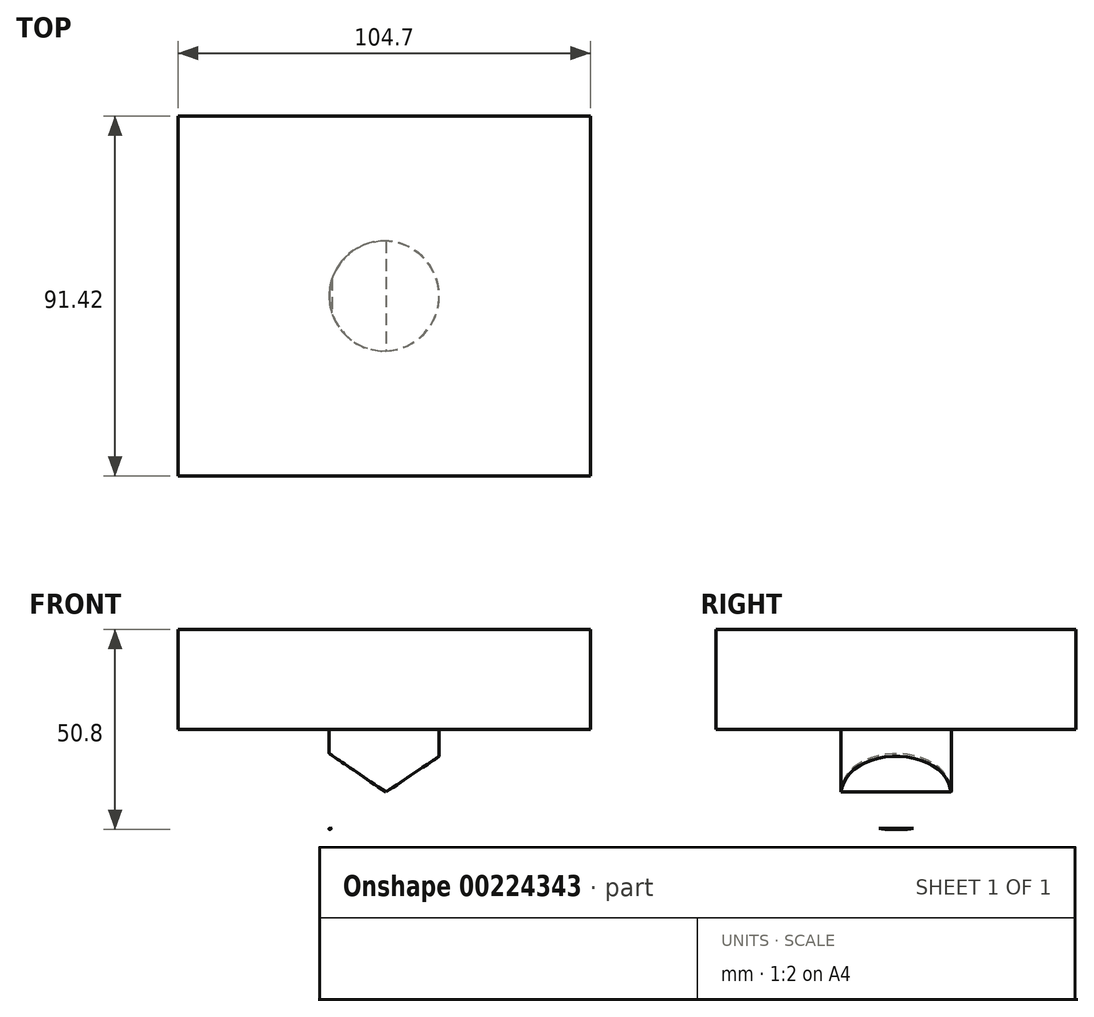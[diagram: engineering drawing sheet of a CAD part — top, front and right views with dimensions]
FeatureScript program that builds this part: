
annotation { "Feature Type Name" : "Feature", "Feature Type Description" : "" }
export const myFeature = defineFeature(function(context is Context, id is Id, definition is map)
    precondition{}
    {
        {
            var Q0;
            Q0=qCreatedBy(makeId("Top.planeOp"),FACE);
            var sketch = newSketch(context, id + "F0", { "sketchPlane" : qUnion([Q0])});
            skLineSegment(sketch, "E0.bottom", {"start": v(52.35, 45.7) * mm, "end": v(-52.35, 45.7) * mm});
            skLineSegment(sketch, "E0.top", {"start": v(52.35, -45.7) * mm, "end": v(-52.35, -45.7) * mm});
            skLineSegment(sketch, "E0.left", {"start": v(52.35, 45.7) * mm, "end": v(52.35, -45.7) * mm});
            skLineSegment(sketch, "E0.right", {"start": v(-52.35, 45.7) * mm, "end": v(-52.35, -45.7) * mm});
            skPoint(sketch, "E0.middle", {"position": v(0, 0) * mm});
            skSolve(sketch);
        }
        {
            var Q0;
            Q0=makeQuery(id+"F0.imprint","IMPRINT",FACE,{"disambiguationData":[TD([[makeQuery(id+"F0.imprint","IMPRINT",EDGE,{"derivedFrom":sQuery(id+"F0.wireOp",EDGE,"E0.bottom")}),1.0]])]});
            extrude(context, id + "F1", {"entities" : qUnion([Q0]), "depth" : 25.4 * mm});
        }
        {
            var Q0;
            Q0=makeQuery(id+"F1.opExtrude","CAP_FACE",FACE,{"disambiguationData":[OSD([sQuery(id+"F0.wireOp",EDGE,"E0.bottom"),sQuery(id+"F0.wireOp",EDGE,"E0.top"),sQuery(id+"F0.wireOp",EDGE,"E0.left"),sQuery(id+"F0.wireOp",EDGE,"E0.right")])],"isStart":true});
            var sketch = newSketch(context, id + "F2", { "sketchPlane" : qUnion([Q0])});
            skCircle(sketch, "E1", {"center": v(0, 0) * mm, "radius": 13.98 * mm});
            skSolve(sketch);
        }
        {
            var Q0;
            Q0 = qSketchRegion(id + "F2", true);
            extrude(context, id + "F3", {"entities" : qUnion([Q0]), "operationType" : NewBodyOperationType.ADD, "depth" : 25.4 * mm});
        }
        {
            var Q0;
            Q0=makeQuery(id+"F1.opExtrude","SWEPT_FACE",FACE,{"disambiguationData":[OSD([sQuery(id+"F0.wireOp",EDGE,"E0.top")])]});
            var sketch = newSketch(context, id + "F4", { "sketchPlane" : qUnion([Q0])});
            skLineSegment(sketch, "E2", {"start": v(13.88, -25.08) * mm, "end": v(-14.08, -6.05) * mm});
            skLineSegment(sketch, "E3", {"start": v(13.88, -25.08) * mm, "end": v(-14.08, -25.08) * mm});
            skLineSegment(sketch, "E4", {"start": v(-14.08, -25.08) * mm, "end": v(-14.08, -6.05) * mm});
            skSolve(sketch);
        }
        {
            var Q0;
            Q0=makeQuery(id+"F4.imprint","IMPRINT",FACE,{"disambiguationData":[TD([[makeQuery(id+"F4.imprint","IMPRINT",EDGE,{"derivedFrom":sQuery(id+"F4.wireOp",EDGE,"E2")}),1.0]])]});
            extrude(context, id + "F5", {"entities" : qUnion([Q0]), "operationType" : NewBodyOperationType.REMOVE, "endBound" : BoundingType.SYMMETRIC, "oppositeDirection" : true, "depth" : 127 * mm});
        }
        {
            var Q0;
            Q0=makeQuery(id+"F1.opExtrude","SWEPT_FACE",FACE,{"disambiguationData":[OSD([sQuery(id+"F0.wireOp",EDGE,"E0.bottom")])]});
            var sketch = newSketch(context, id + "F6", { "sketchPlane" : qUnion([Q0])});
            skLineSegment(sketch, "E5", {"start": v(13.88, -25.48) * mm, "end": v(-14.28, -6.64) * mm});
            skLineSegment(sketch, "E6", {"start": v(13.88, -25.48) * mm, "end": v(-14.28, -25.48) * mm});
            skLineSegment(sketch, "E7", {"start": v(-14.28, -25.48) * mm, "end": v(-14.28, -6.64) * mm});
            skSolve(sketch);
        }
        {
            var Q0;
            Q0=makeQuery(id+"F6.imprint","IMPRINT",FACE,{"disambiguationData":[TD([[makeQuery(id+"F6.imprint","IMPRINT",EDGE,{"derivedFrom":sQuery(id+"F6.wireOp",EDGE,"E5")}),1.0]])]});
            extrude(context, id + "F7", {"entities" : qUnion([Q0]), "operationType" : NewBodyOperationType.REMOVE, "oppositeDirection" : true, "depth" : 127 * mm});
        }
    });
